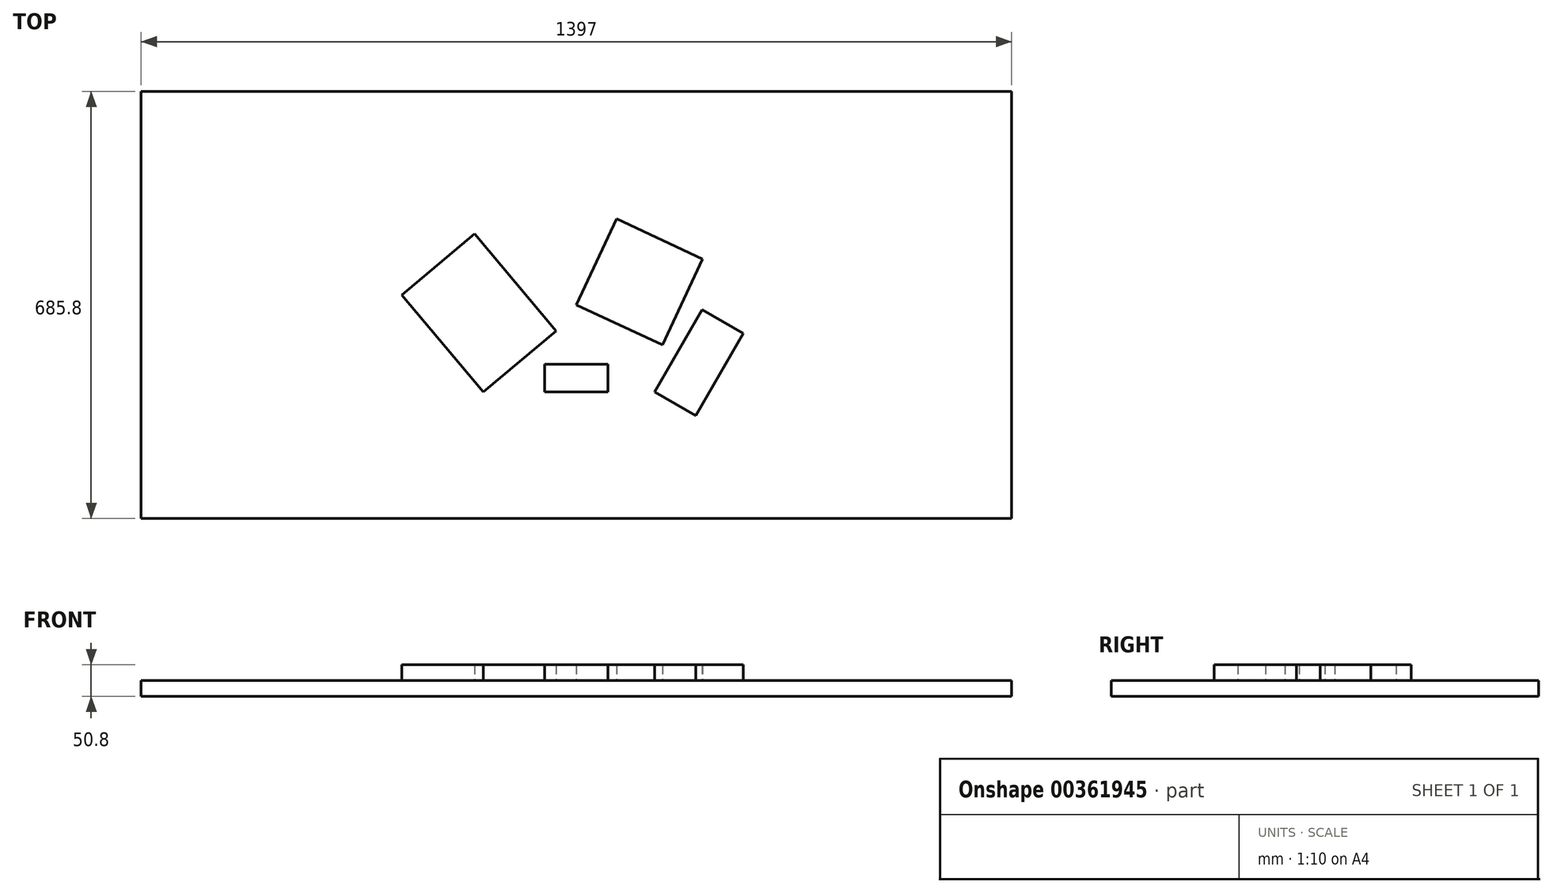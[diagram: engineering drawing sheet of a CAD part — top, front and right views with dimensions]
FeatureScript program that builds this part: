
annotation { "Feature Type Name" : "Feature", "Feature Type Description" : "" }
export const myFeature = defineFeature(function(context is Context, id is Id, definition is map)
    precondition{}
    {
        {
            var Q0;
            Q0=qCreatedBy(makeId("Top.planeOp"),FACE);
            var sketch = newSketch(context, id + "F0", { "sketchPlane" : qUnion([Q0])});
            skLineSegment(sketch, "E0.bottom", {"start": v(698.5, -342.9) * mm, "end": v(-698.5, -342.9) * mm});
            skLineSegment(sketch, "E0.top", {"start": v(698.5, 342.9) * mm, "end": v(-698.5, 342.9) * mm});
            skLineSegment(sketch, "E0.left", {"start": v(698.5, -342.9) * mm, "end": v(698.5, 342.9) * mm});
            skLineSegment(sketch, "E0.right", {"start": v(-698.5, -342.9) * mm, "end": v(-698.5, 342.9) * mm});
            skPoint(sketch, "E0.middle", {"position": v(0, 0) * mm});
            skSolve(sketch);
        }
        {
            var Q0;
            Q0=qSketchRegion(id+"F0",true);
            extrude(context, id + "F1", {"entities" : qUnion([Q0]), "depth" : 25.4 * mm});
        }
        {
            var Q0;
            Q0=makeQuery(id+"F1.opExtrude","CAP_FACE",FACE,{"disambiguationData":[OSD([sQuery(id+"F0.wireOp",EDGE,"E0.bottom"),sQuery(id+"F0.wireOp",EDGE,"E0.top"),sQuery(id+"F0.wireOp",EDGE,"E0.left"),sQuery(id+"F0.wireOp",EDGE,"E0.right")])],"isStart":false});
            var sketch = newSketch(context, id + "F2", { "sketchPlane" : qUnion([Q0])});
            skPoint(sketch, "E1", {"position": v(0, -342.9) * mm});
            skLineSegment(sketch, "E2.bottom", {"start": v(-50.71, -139.69) * mm, "end": v(50.71, -139.69) * mm});
            skLineSegment(sketch, "E2.top", {"start": v(-50.71, -95.25) * mm, "end": v(50.71, -95.25) * mm});
            skLineSegment(sketch, "E2.left", {"start": v(-50.71, -139.69) * mm, "end": v(-50.71, -95.25) * mm});
            skLineSegment(sketch, "E2.right", {"start": v(50.71, -139.69) * mm, "end": v(50.71, -95.25) * mm});
            skLineSegment(sketch, "E3.bottom", {"start": v(-280.04, 15.97) * mm, "end": v(-163.3, 113.93) * mm});
            skLineSegment(sketch, "E3.top", {"start": v(-149.43, -139.69) * mm, "end": v(-32.68, -41.73) * mm});
            skLineSegment(sketch, "E3.left", {"start": v(-280.04, 15.97) * mm, "end": v(-149.43, -139.69) * mm});
            skLineSegment(sketch, "E3.right", {"start": v(-163.3, 113.93) * mm, "end": v(-32.68, -41.73) * mm});
            skLineSegment(sketch, "E4.bottom", {"start": v(201.79, -7.7) * mm, "end": v(267.78, -45.8) * mm});
            skLineSegment(sketch, "E4.top", {"start": v(125.59, -139.69) * mm, "end": v(191.58, -177.79) * mm});
            skLineSegment(sketch, "E4.left", {"start": v(201.79, -7.7) * mm, "end": v(125.59, -139.69) * mm});
            skLineSegment(sketch, "E4.right", {"start": v(267.78, -45.8) * mm, "end": v(191.58, -177.79) * mm});
            skLineSegment(sketch, "E5.bottom", {"start": v(64.4, 138.12) * mm, "end": v(202.53, 73.71) * mm});
            skLineSegment(sketch, "E5.top", {"start": v(0, 0) * mm, "end": v(138.12, -64.4) * mm});
            skLineSegment(sketch, "E5.left", {"start": v(64.4, 138.12) * mm, "end": v(0, 0) * mm});
            skLineSegment(sketch, "E5.right", {"start": v(202.53, 73.71) * mm, "end": v(138.12, -64.4) * mm});
            skPoint(sketch, "E6", {"position": v(69.06, -32.2) * mm});
            skPoint(sketch, "E7", {"position": v(163.69, -73.7) * mm});
            skPoint(sketch, "E8", {"position": v(-91.06, -90.7) * mm});
            skPoint(sketch, "E9", {"position": v(-98, 36.1) * mm});
            skPoint(sketch, "E10", {"position": v(-170.42, 0) * mm});
            skPoint(sketch, "E11", {"position": v(105.5, 31.75) * mm});
            skPoint(sketch, "E12", {"position": v(0, -95.25) * mm});
            skSolve(sketch);
        }
        {
            var Q0;
            Q0=qSketchRegion(id+"F2",true);
            extrude(context, id + "F3", {"entities" : qUnion([Q0]), "depth" : 25.4 * mm});
        }
    });
